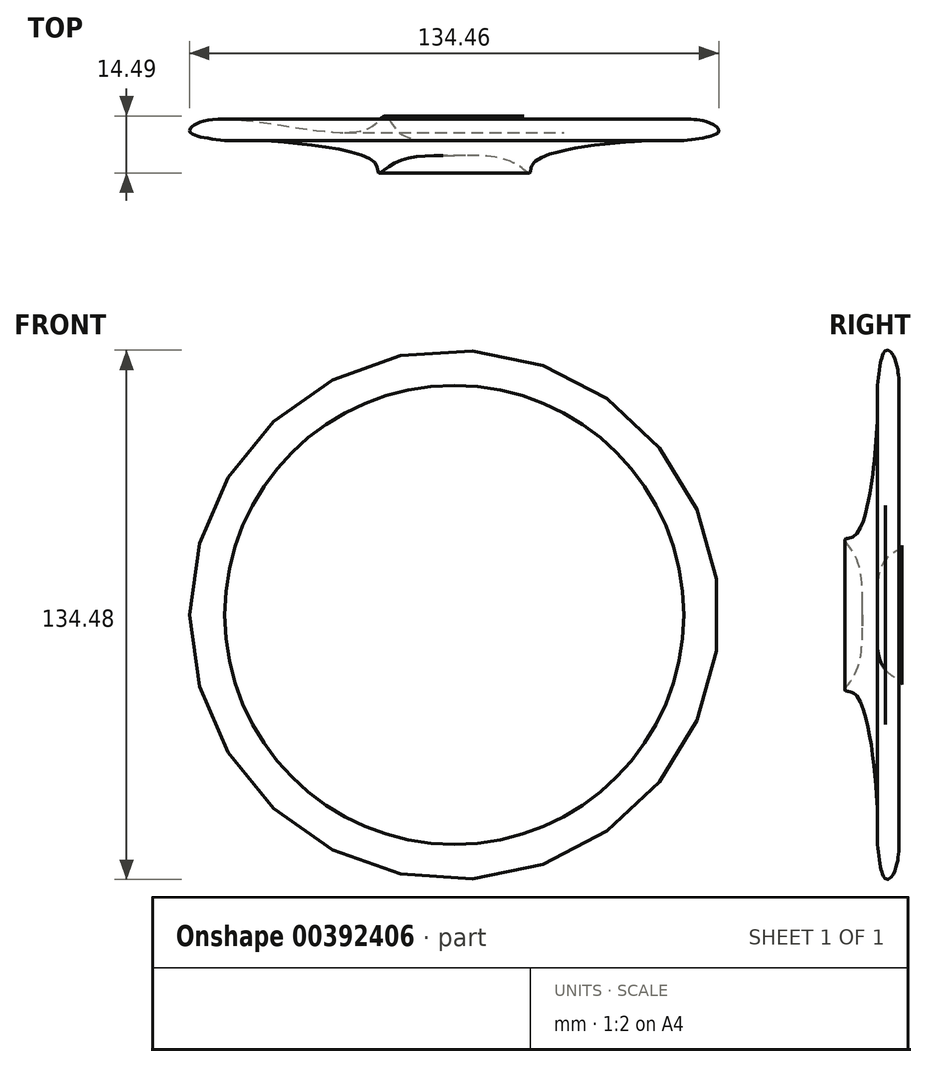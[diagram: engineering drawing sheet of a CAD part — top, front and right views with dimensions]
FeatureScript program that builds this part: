
annotation { "Feature Type Name" : "Feature", "Feature Type Description" : "" }
export const myFeature = defineFeature(function(context is Context, id is Id, definition is map)
    precondition{}
    {
        {
            var Q0;
            Q0=qCreatedBy(makeId("Top.planeOp"),FACE);
            var sketch = newSketch(context, id + "F0", { "sketchPlane" : qUnion([Q0])});
            skFitSpline(sketch, "E0", {"points": [v(-58.32, 0) * mm, v(-49.29, 0) * mm, v(-20.2, -5.59) * mm, v(-19.22, -8.21) * mm, v(-14.95, -5.59) * mm, v(0, -3.78) * mm], "startDerivative": vector(34.63, 1.85) * mm, "endDerivative": vector(69.87, -0.73) * mm});
            skFitSpline(sketch, "E1", {"points": [v(-58.32, 0) * mm, v(-67.2, 2.3) * mm, v(-60.62, 5.42) * mm, v(-22.5, 2.8) * mm, v(-17.58, 6.24) * mm, v(-13.8, 1.97) * mm, v(0, 0) * mm], "startDerivative": vector(-85.2, 10.75) * mm, "endDerivative": vector(88.93, 3.55) * mm});
            skLineSegment(sketch, "E2", {"start": v(0, 0) * mm, "end": v(0, -3.78) * mm});
            skSolve(sketch);
        }
        {
            var Q0;
            Q0 = qSketchRegion(id + "F0", true);
            var Q1;
            Q1=sQuery(id+"F0.wireOp",EDGE,"E2");
            revolve(context, id + "F1", {"entities" : qUnion([Q0]), "axis" : qUnion([Q1]), "revolveType" : RevolveType.FULL});
        }
    });
